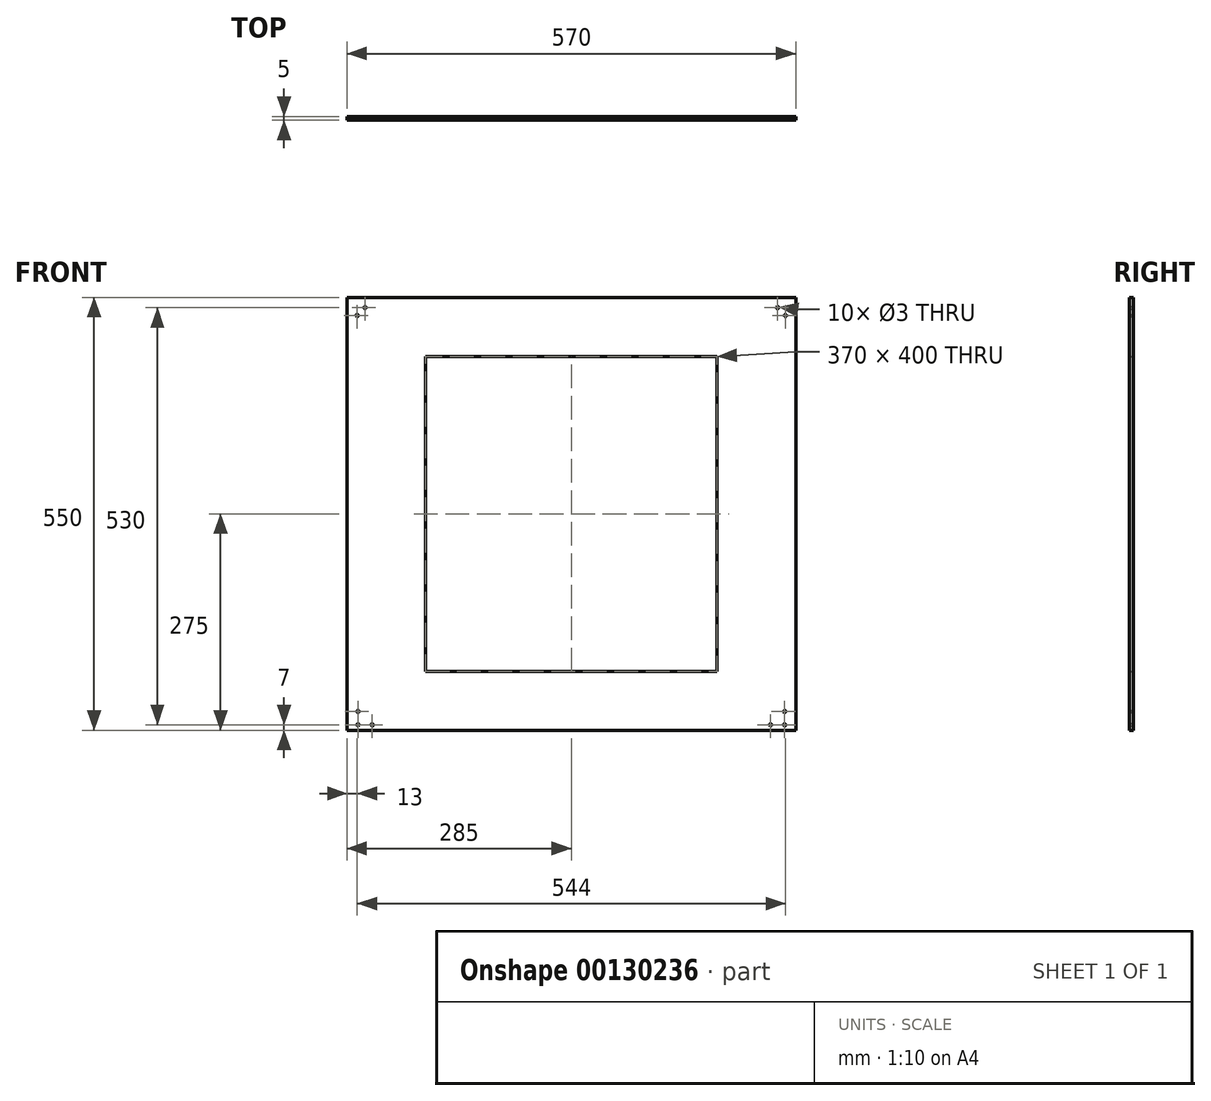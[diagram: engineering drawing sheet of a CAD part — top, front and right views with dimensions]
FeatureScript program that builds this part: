
annotation { "Feature Type Name" : "Feature", "Feature Type Description" : "" }
export const myFeature = defineFeature(function(context is Context, id is Id, definition is map)
    precondition{}
    {
        {
            var Q0;
            Q0=qCreatedBy(makeId("Front.planeOp"),FACE);
            var sketch = newSketch(context, id + "F0", { "sketchPlane" : qUnion([Q0])});
            skLineSegment(sketch, "E0.bottom", {"start": v(-285, -275) * mm, "end": v(285, -275) * mm});
            skLineSegment(sketch, "E0.top", {"start": v(-285, 275) * mm, "end": v(285, 275) * mm});
            skLineSegment(sketch, "E0.left", {"start": v(-285, -275) * mm, "end": v(-285, 275) * mm});
            skLineSegment(sketch, "E0.right", {"start": v(285, -275) * mm, "end": v(285, 275) * mm});
            skPoint(sketch, "E0.middle", {"position": v(0, 0) * mm});
            skLineSegment(sketch, "E1.bottom", {"start": v(185, 200) * mm, "end": v(-185, 200) * mm});
            skLineSegment(sketch, "E1.top", {"start": v(185, -200) * mm, "end": v(-185, -200) * mm});
            skLineSegment(sketch, "E1.left", {"start": v(185, 200) * mm, "end": v(185, -200) * mm});
            skLineSegment(sketch, "E1.right", {"start": v(-185, 200) * mm, "end": v(-185, -200) * mm});
            skCircle(sketch, "E2", {"center": v(-271, -251) * mm, "radius": 1.5 * mm});
            skCircle(sketch, "E3", {"center": v(-253, -268) * mm, "radius": 1.5 * mm});
            skCircle(sketch, "E4", {"center": v(-271, -268) * mm, "radius": 1.5 * mm});
            skCircle(sketch, "E5.MirrorC", {"center": v(271, -251) * mm, "radius": 1.5 * mm});
            skCircle(sketch, "E6.MirrorC", {"center": v(271, -268) * mm, "radius": 1.5 * mm});
            skCircle(sketch, "E7.MirrorC", {"center": v(253, -268) * mm, "radius": 1.5 * mm});
            skCircle(sketch, "E8", {"center": v(-262, 262) * mm, "radius": 1.5 * mm});
            skCircle(sketch, "E9", {"center": v(-272, 252) * mm, "radius": 1.5 * mm});
            skCircle(sketch, "E10.MirrorC", {"center": v(262, 262) * mm, "radius": 1.5 * mm});
            skCircle(sketch, "E11.MirrorC", {"center": v(272, 252) * mm, "radius": 1.5 * mm});
            skSolve(sketch);
        }
        {
            var Q0;
            Q0=makeQuery(id+"F0.imprint","IMPRINT",FACE,{"disambiguationData":[TD([[makeQuery(id+"F0.imprint","IMPRINT",EDGE,{"derivedFrom":sQuery(id+"F0.wireOp",EDGE,"E0.bottom")}),1.0]])]});
            extrude(context, id + "F1", {"entities" : qUnion([Q0]), "endBound" : BoundingType.SYMMETRIC, "depth" : 5 * mm});
        }
    });
